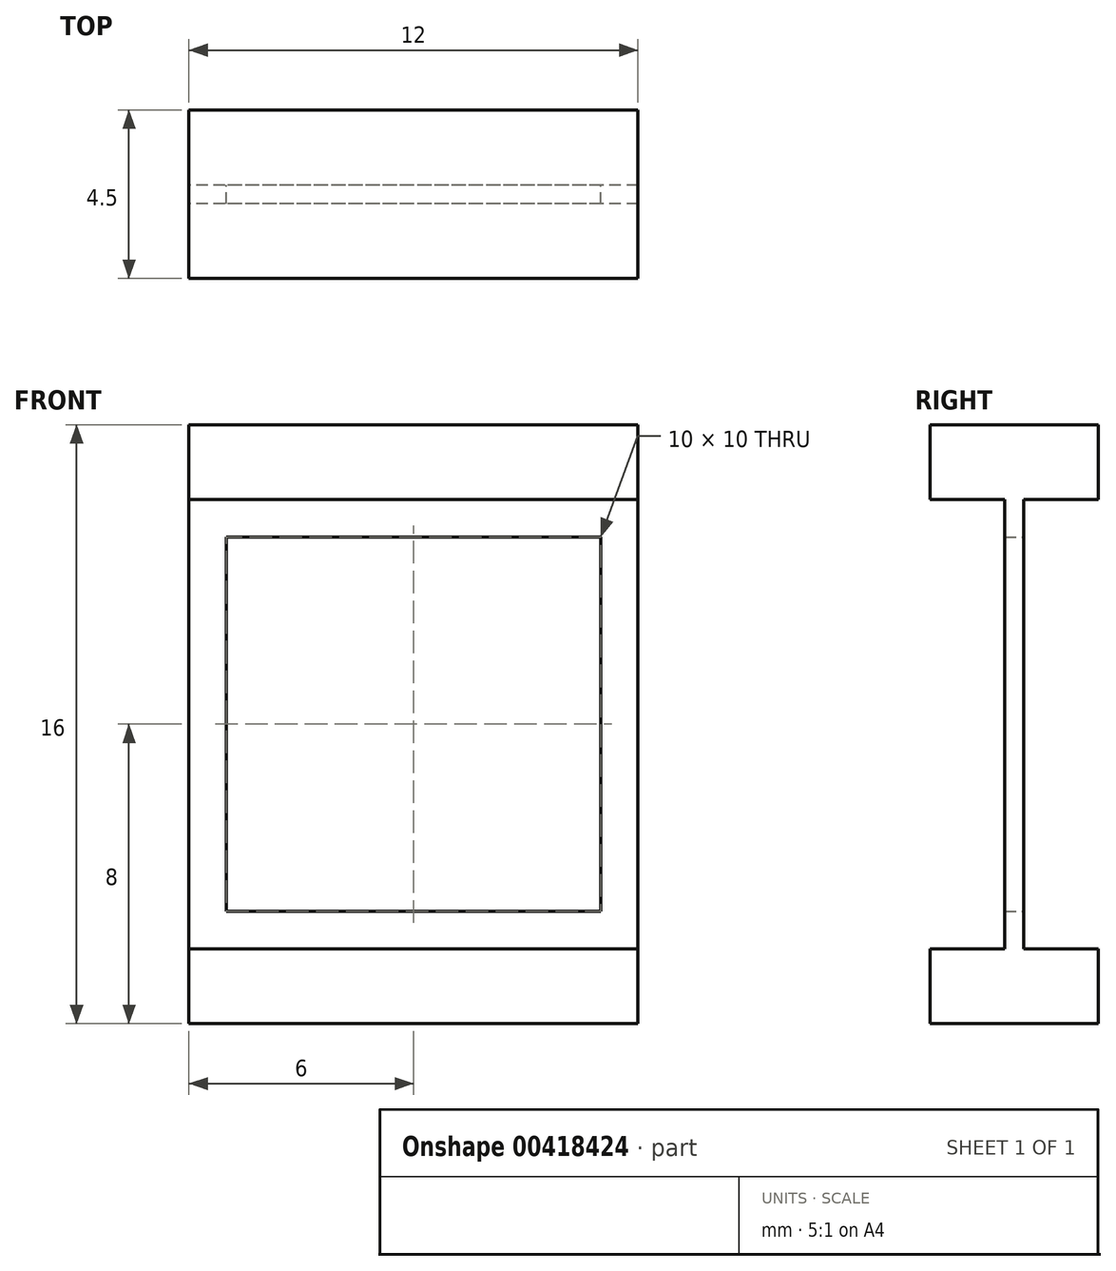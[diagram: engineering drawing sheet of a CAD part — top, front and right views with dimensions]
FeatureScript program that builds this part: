
annotation { "Feature Type Name" : "Feature", "Feature Type Description" : "" }
export const myFeature = defineFeature(function(context is Context, id is Id, definition is map)
    precondition{}
    {
        {
            var Q0;
            Q0=qCreatedBy(makeId("Right.planeOp"),FACE);
            var sketch = newSketch(context, id + "F0", { "sketchPlane" : qUnion([Q0])});
            skLineSegment(sketch, "E0", {"start": v(-2.25, 16) * mm, "end": v(2.25, 16) * mm});
            skLineSegment(sketch, "E1", {"start": v(2.25, 16) * mm, "end": v(2.25, 14) * mm});
            skLineSegment(sketch, "E2", {"start": v(2.25, 14) * mm, "end": v(0.25, 14) * mm});
            skLineSegment(sketch, "E3", {"start": v(0.25, 14) * mm, "end": v(0.25, 2) * mm});
            skLineSegment(sketch, "E4", {"start": v(0.25, 2) * mm, "end": v(2.25, 2) * mm});
            skLineSegment(sketch, "E5", {"start": v(2.25, 2) * mm, "end": v(2.25, 0) * mm});
            skLineSegment(sketch, "E6", {"start": v(2.25, 0) * mm, "end": v(-2.25, 0) * mm});
            skLineSegment(sketch, "E7", {"start": v(-2.25, 0) * mm, "end": v(-2.25, 2) * mm});
            skLineSegment(sketch, "E8", {"start": v(-2.25, 2) * mm, "end": v(-0.25, 2) * mm});
            skLineSegment(sketch, "E9", {"start": v(-0.25, 2) * mm, "end": v(-0.25, 14) * mm});
            skLineSegment(sketch, "E10", {"start": v(-0.25, 14) * mm, "end": v(-2.25, 14) * mm});
            skLineSegment(sketch, "E11", {"start": v(-2.25, 14) * mm, "end": v(-2.25, 16) * mm});
            skSolve(sketch);
        }
        {
            var Q0;
            Q0 = qSketchRegion(id + "F0", true);
            extrude(context, id + "F1", {"entities" : qUnion([Q0]), "depth" : 12 * mm});
        }
        {
            var Q0;
            Q0=makeQuery(id+"F1.opExtrude","SWEPT_FACE",FACE,{"disambiguationData":[OSD([sQuery(id+"F0.wireOp",EDGE,"E3")])]});
            var sketch = newSketch(context, id + "F2", { "sketchPlane" : qUnion([Q0])});
            skLineSegment(sketch, "E12.bottom", {"start": v(-11, 13) * mm, "end": v(-1, 13) * mm});
            skLineSegment(sketch, "E12.top", {"start": v(-11, 3) * mm, "end": v(-1, 3) * mm});
            skLineSegment(sketch, "E12.left", {"start": v(-11, 13) * mm, "end": v(-11, 3) * mm});
            skLineSegment(sketch, "E12.right", {"start": v(-1, 13) * mm, "end": v(-1, 3) * mm});
            skSolve(sketch);
        }
        {
            var Q0;
            Q0 = qSketchRegion(id + "F2", true);
            extrude(context, id + "F3", {"entities" : qUnion([Q0]), "operationType" : NewBodyOperationType.REMOVE, "endBound" : BoundingType.UP_TO_NEXT, "oppositeDirection" : true, "depth" : 25 * mm});
        }
    });
